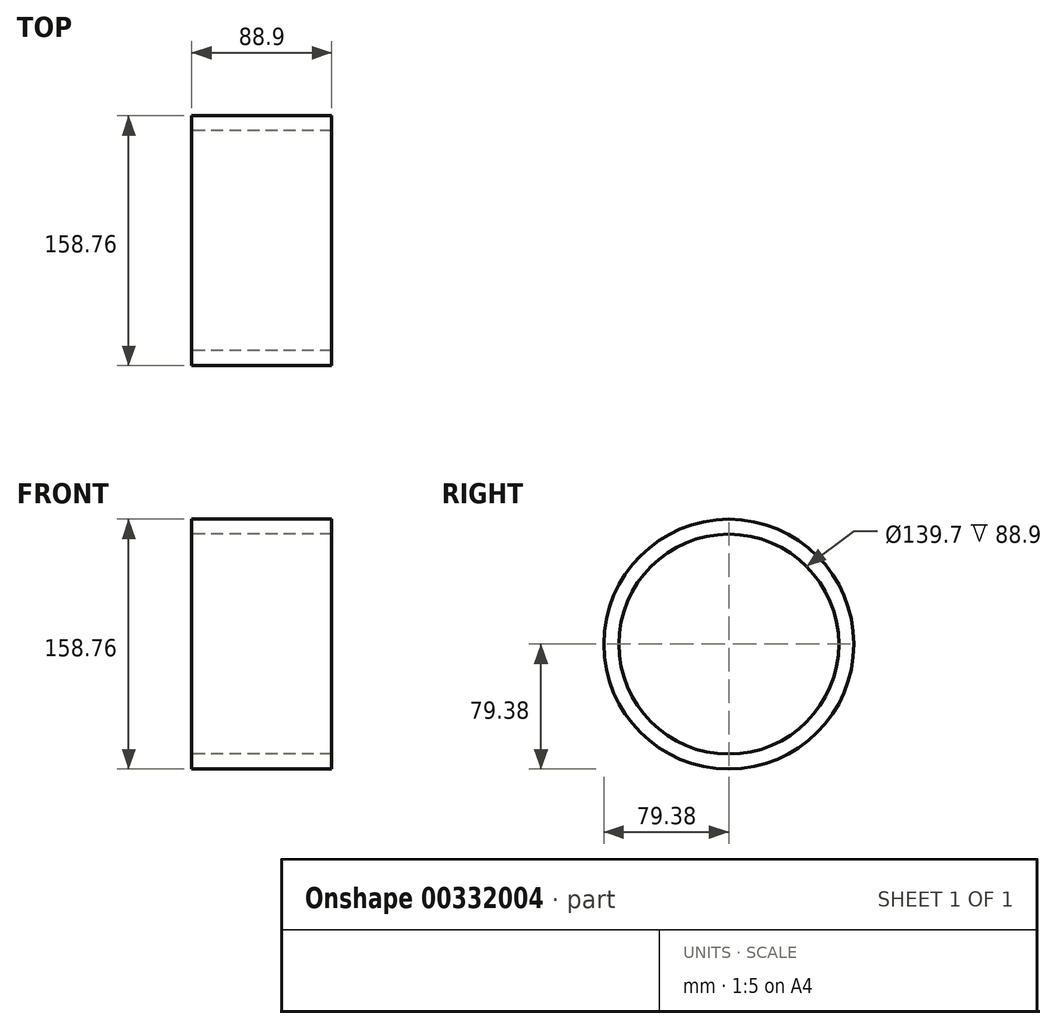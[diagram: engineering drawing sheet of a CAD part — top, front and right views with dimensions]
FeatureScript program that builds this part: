
annotation { "Feature Type Name" : "Feature", "Feature Type Description" : "" }
export const myFeature = defineFeature(function(context is Context, id is Id, definition is map)
    precondition{}
    {
        {
            var Q0;
            Q0=qCreatedBy(makeId("Right.planeOp"),FACE);
            var sketch = newSketch(context, id + "F0", { "sketchPlane" : qUnion([Q0])});
            skCircle(sketch, "E0", {"center": v(0, 0) * mm, "radius": 69.85 * mm});
            skCircle(sketch, "E1", {"center": v(0, 0) * mm, "radius": 79.38 * mm});
            skSolve(sketch);
        }
        {
            var Q0;
            Q0 = qSketchRegion(id + "F0", true);
            extrude(context, id + "F1", {"entities" : qUnion([Q0]), "endBound" : BoundingType.SYMMETRIC, "depth" : 88.9 * mm});
        }
    });
